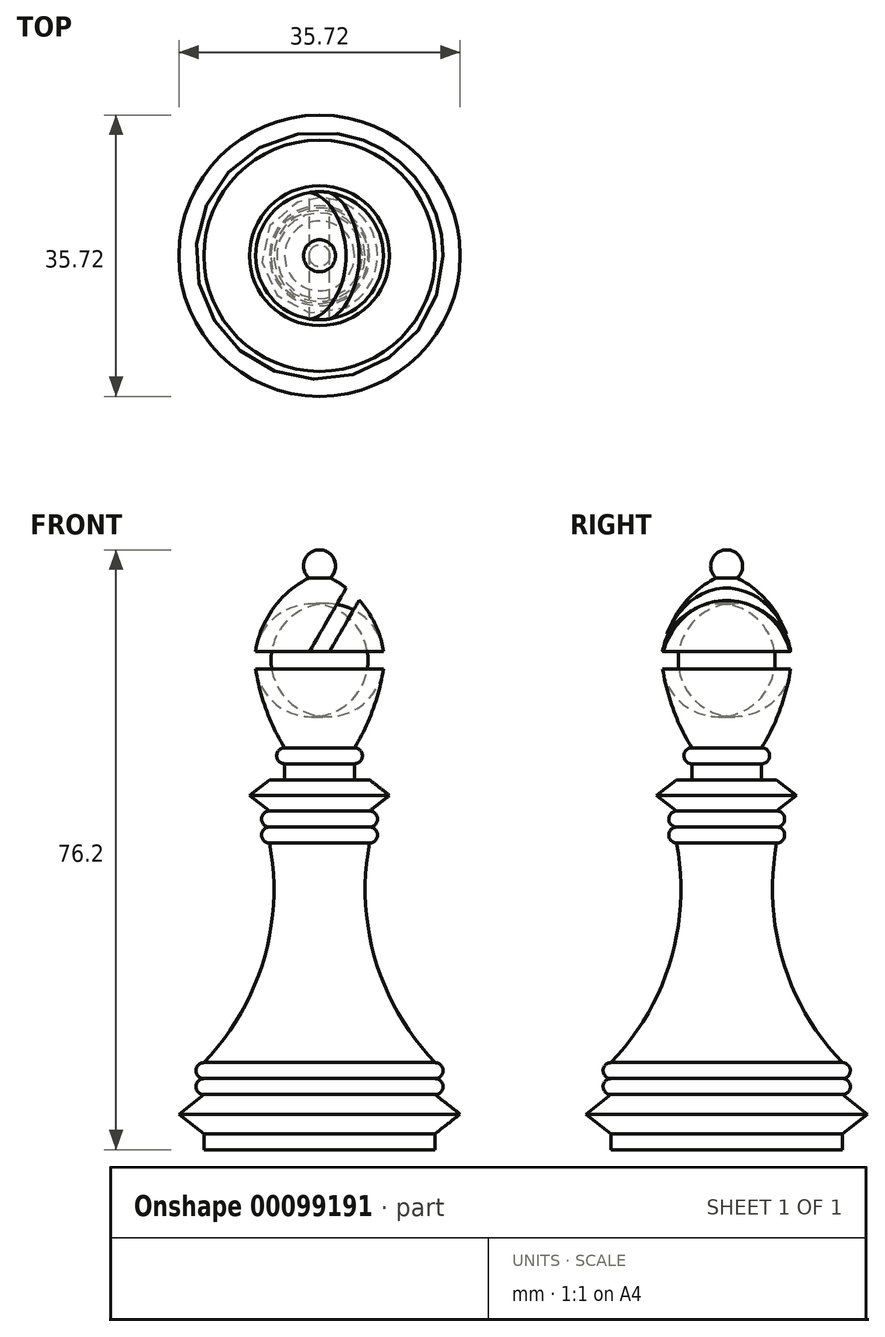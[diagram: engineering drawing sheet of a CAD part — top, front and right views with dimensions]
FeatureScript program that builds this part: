
annotation { "Feature Type Name" : "Feature", "Feature Type Description" : "" }
export const myFeature = defineFeature(function(context is Context, id is Id, definition is map)
    precondition{}
    {
        {
            var Q0;
            Q0=qCreatedBy(makeId("Front.planeOp"),FACE);
            var sketch = newSketch(context, id + "F0", { "sketchPlane" : qUnion([Q0])});
            skLineSegment(sketch, "E0", {"start": v(0, 76.2) * mm, "end": v(0, 0) * mm});
            skLineSegment(sketch, "E1", {"start": v(0, 0) * mm, "end": v(14.68, 0) * mm});
            skLineSegment(sketch, "E2", {"start": v(14.68, 0) * mm, "end": v(14.68, 2.03) * mm});
            skLineSegment(sketch, "E3", {"start": v(14.68, 2.03) * mm, "end": v(17.86, 4.51) * mm});
            skLineSegment(sketch, "E4", {"start": v(17.86, 4.51) * mm, "end": v(14.68, 7) * mm});
            skArc(sketch, "E5", {"start": v(14.68, 7) * mm, "mid": v(15.7, 8) * mm, "end": v(14.68, 9.03) * mm});
            skArc(sketch, "E6", {"start": v(14.68, 9.03) * mm, "mid": v(15.7, 10.04) * mm, "end": v(14.68, 11.06) * mm});
            skArc(sketch, "E7", {"start": v(6.35, 38.96) * mm, "mid": v(7.13, 24) * mm, "end": v(14.68, 11.06) * mm});
            skArc(sketch, "E8", {"start": v(6.35, 38.96) * mm, "mid": v(7.37, 39.97) * mm, "end": v(6.35, 40.99) * mm});
            skArc(sketch, "E9", {"start": v(6.35, 40.99) * mm, "mid": v(7.37, 42) * mm, "end": v(6.35, 43.02) * mm});
            skLineSegment(sketch, "E10", {"start": v(6.35, 43.02) * mm, "end": v(8.89, 45) * mm});
            skLineSegment(sketch, "E11", {"start": v(8.89, 45) * mm, "end": v(6.35, 47) * mm});
            skLineSegment(sketch, "E12", {"start": v(6.35, 47) * mm, "end": v(4.43, 47) * mm});
            skLineSegment(sketch, "E13", {"start": v(4.43, 46.99) * mm, "end": v(4.43, 49.02) * mm});
            skArc(sketch, "E14", {"start": v(4.43, 49.02) * mm, "mid": v(5.45, 50.04) * mm, "end": v(4.43, 51.05) * mm});
            skArc(sketch, "E15", {"start": v(1.34, 72.64) * mm, "mid": v(1.9, 74.89) * mm, "end": v(0, 76.2) * mm});
            skLineSegment(sketch, "E16", {"start": v(0, 76.2) * mm, "end": v(-4.84, 76.2) * mm, "construction": true});
            skArc(sketch, "E17", {"start": v(8.13, 63.3) * mm, "mid": v(5.86, 68.78) * mm, "end": v(1.34, 72.64) * mm});
            skArc(sketch, "E18", {"start": v(8.13, 63.3) * mm, "mid": v(8.21, 62.18) * mm, "end": v(8.13, 61.07) * mm});
            skArc(sketch, "E19", {"start": v(8.13, 61.07) * mm, "mid": v(6.78, 55.88) * mm, "end": v(4.43, 51.05) * mm});
            skLineSegment(sketch, "E20", {"start": v(14.68, 9.03) * mm, "end": v(11.62, 9.03) * mm, "construction": true});
            skLineSegment(sketch, "E21", {"start": v(14.68, 11.06) * mm, "end": v(11.64, 11.06) * mm, "construction": true});
            skLineSegment(sketch, "E22", {"start": v(6.35, 40.99) * mm, "end": v(1.05, 40.99) * mm, "construction": true});
            skLineSegment(sketch, "E23", {"start": v(6.35, 43.02) * mm, "end": v(0.76, 43.02) * mm, "construction": true});
            skLineSegment(sketch, "E24", {"start": v(4.43, 51.05) * mm, "end": v(1.11, 51.05) * mm, "construction": true});
            skSolve(sketch);
        }
        {
            var Q0;
            Q0=qSketchRegion(id+"F0",true);
            var Q1;
            Q1=sQuery(id+"F0.wireOp",EDGE,"E0");
            revolve(context, id + "F1", {"entities" : qUnion([Q0]), "axis" : qUnion([Q1]), "revolveType" : RevolveType.FULL});
        }
        {
            var Q0;
            Q0=qCreatedBy(makeId("Front.planeOp"),FACE);
            var sketch = newSketch(context, id + "F2", { "sketchPlane" : qUnion([Q0])});
            skLineSegment(sketch, "E25", {"start": v(-1.27, 63.3) * mm, "end": v(1.27, 63.3) * mm});
            skLineSegment(sketch, "E26", {"start": v(1.27, 63.3) * mm, "end": v(6.67, 72.64) * mm});
            skLineSegment(sketch, "E27", {"start": v(6.67, 72.64) * mm, "end": v(4.13, 72.64) * mm});
            skLineSegment(sketch, "E28", {"start": v(4.13, 72.64) * mm, "end": v(-1.27, 63.3) * mm});
            skPoint(sketch, "E29", {"position": v(0, 63.3) * mm});
            skSolve(sketch);
        }
        {
            var Q0;
            Q0=qSketchRegion(id+"F2",true);
            extrude(context, id + "F3", {"entities" : qUnion([Q0]), "operationType" : NewBodyOperationType.REMOVE, "endBound" : BoundingType.SYMMETRIC, "depth" : 25.4 * mm});
        }
    });
